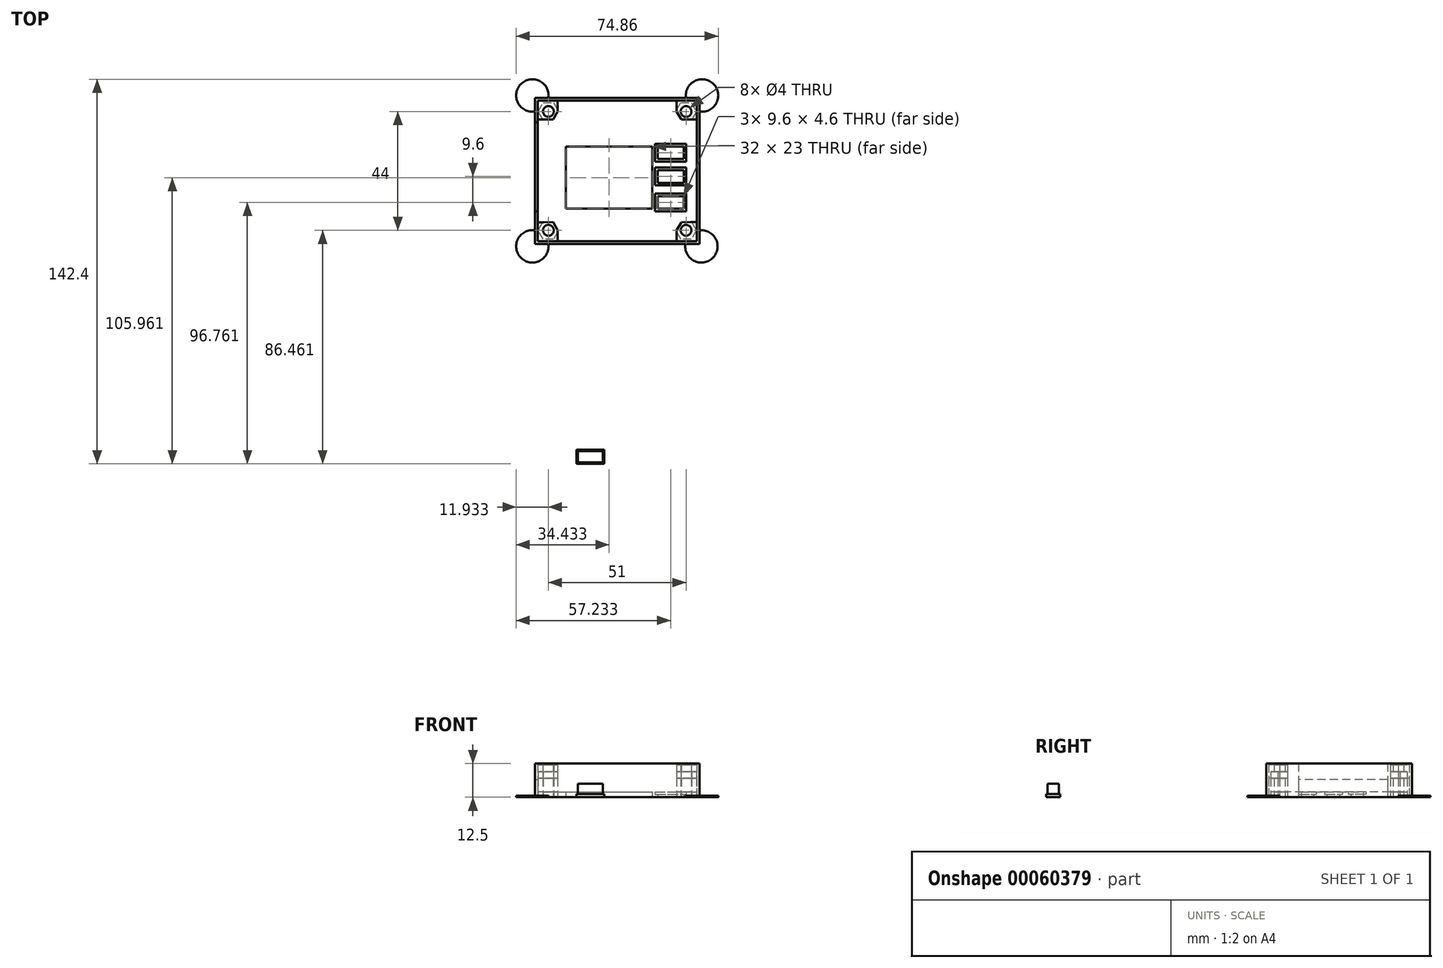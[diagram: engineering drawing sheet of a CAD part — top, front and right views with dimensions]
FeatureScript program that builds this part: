
annotation { "Feature Type Name" : "Feature", "Feature Type Description" : "" }
export const myFeature = defineFeature(function(context is Context, id is Id, definition is map)
    precondition{}
    {
        {
            var Q0;
            Q0=qCreatedBy(makeId("Top.planeOp"),FACE);
            var sketch = newSketch(context, id + "F0", { "sketchPlane" : qUnion([Q0])});
            skCircle(sketch, "E0.cCircle", {"center": v(0, 0) * mm, "radius": 3 * mm, "construction": true});
            skLineSegment(sketch, "E0.0", {"start": v(1.73, 3) * mm, "end": v(3.46, 0) * mm});
            skLineSegment(sketch, "E0.1", {"start": v(3.46, 0) * mm, "end": v(1.74, -3) * mm});
            skLineSegment(sketch, "E0.2", {"start": v(1.74, -3) * mm, "end": v(-1.73, -3) * mm});
            skLineSegment(sketch, "E0.3", {"start": v(-1.73, -3) * mm, "end": v(-3.46, 0) * mm});
            skLineSegment(sketch, "E0.4", {"start": v(-3.46, 0) * mm, "end": v(-1.74, 3) * mm});
            skLineSegment(sketch, "E0.5", {"start": v(-1.74, 3) * mm, "end": v(1.73, 3) * mm});
            skPoint(sketch, "E0.0.midPoint", {"position": v(2.6, 1.5) * mm});
            skCircle(sketch, "E1", {"center": v(0, 0) * mm, "radius": 1.5 * mm});
            skLineSegment(sketch, "E2.bottom", {"start": v(-2.76, 81.41) * mm, "end": v(56.24, 81.41) * mm});
            skLineSegment(sketch, "E2.top", {"start": v(-2.76, 29.41) * mm, "end": v(56.24, 29.41) * mm});
            skLineSegment(sketch, "E2.left", {"start": v(-2.76, 81.41) * mm, "end": v(-2.76, 29.41) * mm});
            skLineSegment(sketch, "E2.right", {"start": v(56.24, 81.41) * mm, "end": v(56.24, 29.41) * mm});
            skPoint(sketch, "E3.0.midPoint", {"position": v(3.84, 78.92) * mm});
            skLineSegment(sketch, "E3.3", {"start": v(-0.48, 74.4) * mm, "end": v(-2.22, 77.4) * mm, "construction": true});
            skLineSegment(sketch, "E3.2", {"start": v(2.98, 74.41) * mm, "end": v(-0.48, 74.4) * mm});
            skLineSegment(sketch, "E3.1", {"start": v(4.7, 77.42) * mm, "end": v(2.98, 74.41) * mm});
            skLineSegment(sketch, "E3.0", {"start": v(2.97, 80.41) * mm, "end": v(4.7, 77.42) * mm, "construction": true});
            skLineSegment(sketch, "E3.4", {"start": v(-2.22, 77.4) * mm, "end": v(-0.5, 80.4) * mm, "construction": true});
            skLineSegment(sketch, "E3.5", {"start": v(-0.5, 80.4) * mm, "end": v(2.97, 80.41) * mm, "construction": true});
            skCircle(sketch, "E4", {"center": v(1.24, 77.41) * mm, "radius": 1.5 * mm, "construction": true});
            skCircle(sketch, "E3.cCircle", {"center": v(1.24, 77.41) * mm, "radius": 3 * mm, "construction": true});
            skPoint(sketch, "E5.0.midPoint", {"position": v(3.84, 34.92) * mm});
            skLineSegment(sketch, "E5.3", {"start": v(-0.48, 30.4) * mm, "end": v(-2.22, 33.4) * mm, "construction": true});
            skLineSegment(sketch, "E5.2", {"start": v(2.98, 30.41) * mm, "end": v(-0.48, 30.4) * mm, "construction": true});
            skLineSegment(sketch, "E5.1", {"start": v(4.7, 33.42) * mm, "end": v(2.98, 30.41) * mm, "construction": true});
            skLineSegment(sketch, "E5.0", {"start": v(2.97, 36.41) * mm, "end": v(4.7, 33.42) * mm});
            skLineSegment(sketch, "E5.4", {"start": v(-2.22, 33.4) * mm, "end": v(-0.5, 36.4) * mm, "construction": true});
            skLineSegment(sketch, "E5.5", {"start": v(-0.5, 36.4) * mm, "end": v(2.97, 36.41) * mm});
            skCircle(sketch, "E6", {"center": v(1.24, 33.41) * mm, "radius": 1.5 * mm, "construction": true});
            skCircle(sketch, "E5.cCircle", {"center": v(1.24, 33.41) * mm, "radius": 3 * mm, "construction": true});
            skPoint(sketch, "E7.0.midPoint", {"position": v(54.84, 78.92) * mm});
            skLineSegment(sketch, "E7.3", {"start": v(50.52, 74.4) * mm, "end": v(48.78, 77.4) * mm});
            skLineSegment(sketch, "E7.2", {"start": v(53.98, 74.41) * mm, "end": v(50.52, 74.4) * mm});
            skLineSegment(sketch, "E7.1", {"start": v(55.7, 77.42) * mm, "end": v(53.98, 74.41) * mm, "construction": true});
            skLineSegment(sketch, "E7.0", {"start": v(53.97, 80.41) * mm, "end": v(55.7, 77.42) * mm, "construction": true});
            skLineSegment(sketch, "E7.4", {"start": v(48.78, 77.4) * mm, "end": v(50.5, 80.4) * mm, "construction": true});
            skLineSegment(sketch, "E7.5", {"start": v(50.5, 80.4) * mm, "end": v(53.97, 80.41) * mm, "construction": true});
            skCircle(sketch, "E8", {"center": v(52.24, 77.41) * mm, "radius": 1.5 * mm, "construction": true});
            skCircle(sketch, "E7.cCircle", {"center": v(52.24, 77.41) * mm, "radius": 3 * mm, "construction": true});
            skPoint(sketch, "E9.0.midPoint", {"position": v(54.84, 34.92) * mm});
            skLineSegment(sketch, "E9.3", {"start": v(50.52, 30.4) * mm, "end": v(48.78, 33.4) * mm, "construction": true});
            skLineSegment(sketch, "E9.2", {"start": v(53.98, 30.41) * mm, "end": v(50.52, 30.4) * mm, "construction": true});
            skLineSegment(sketch, "E9.1", {"start": v(55.7, 33.42) * mm, "end": v(53.98, 30.41) * mm, "construction": true});
            skLineSegment(sketch, "E9.0", {"start": v(53.97, 36.41) * mm, "end": v(55.7, 33.42) * mm, "construction": true});
            skLineSegment(sketch, "E9.4", {"start": v(48.78, 33.4) * mm, "end": v(50.5, 36.4) * mm});
            skLineSegment(sketch, "E9.5", {"start": v(50.5, 36.4) * mm, "end": v(53.97, 36.41) * mm});
            skCircle(sketch, "E10", {"center": v(52.24, 33.41) * mm, "radius": 1.5 * mm, "construction": true});
            skCircle(sketch, "E9.cCircle", {"center": v(52.24, 33.41) * mm, "radius": 3 * mm, "construction": true});
            skLineSegment(sketch, "E11", {"start": v(48.78, 33.4) * mm, "end": v(48.78, 29.41) * mm});
            skLineSegment(sketch, "E12", {"start": v(53.97, 36.41) * mm, "end": v(56.24, 36.41) * mm});
            skCircle(sketch, "E13.0", {"center": v(52.24, 33.41) * mm, "radius": 2 * mm});
            skLineSegment(sketch, "E14.0", {"start": v(50.34, 30.1) * mm, "end": v(48.52, 33.25) * mm});
            skLineSegment(sketch, "E14.1", {"start": v(54.15, 30.11) * mm, "end": v(50.34, 30.1) * mm});
            skLineSegment(sketch, "E14.2", {"start": v(56.05, 33.42) * mm, "end": v(54.15, 30.11) * mm});
            skLineSegment(sketch, "E14.3", {"start": v(54.23, 36.56) * mm, "end": v(56.05, 33.42) * mm});
            skLineSegment(sketch, "E15", {"start": v(4.7, 33.42) * mm, "end": v(4.7, 29.41) * mm});
            skLineSegment(sketch, "E16", {"start": v(-0.5, 36.4) * mm, "end": v(-2.76, 36.4) * mm});
            skLineSegment(sketch, "E17", {"start": v(-0.48, 74.4) * mm, "end": v(-2.76, 74.4) * mm});
            skLineSegment(sketch, "E18", {"start": v(4.7, 77.42) * mm, "end": v(4.7, 81.41) * mm});
            skLineSegment(sketch, "E19", {"start": v(53.98, 74.41) * mm, "end": v(56.24, 74.42) * mm});
            skLineSegment(sketch, "E20", {"start": v(48.78, 77.4) * mm, "end": v(48.78, 81.41) * mm});
            skCircle(sketch, "E21.0", {"center": v(52.24, 77.41) * mm, "radius": 2 * mm});
            skCircle(sketch, "E22.0", {"center": v(1.24, 77.41) * mm, "radius": 2 * mm});
            skCircle(sketch, "E23.0", {"center": v(1.24, 33.41) * mm, "radius": 2 * mm});
            skLineSegment(sketch, "E24.0", {"start": v(3.14, 80.71) * mm, "end": v(4.97, 77.57) * mm});
            skLineSegment(sketch, "E24.1", {"start": v(-0.67, 80.7) * mm, "end": v(3.14, 80.71) * mm});
            skLineSegment(sketch, "E24.2", {"start": v(-2.57, 77.4) * mm, "end": v(-0.67, 80.7) * mm});
            skLineSegment(sketch, "E24.3", {"start": v(-0.74, 74.26) * mm, "end": v(-2.57, 77.4) * mm});
            skLineSegment(sketch, "E25.0", {"start": v(-2.57, 33.4) * mm, "end": v(-0.76, 36.56) * mm});
            skLineSegment(sketch, "E25.1", {"start": v(-0.66, 30.1) * mm, "end": v(-2.57, 33.4) * mm});
            skLineSegment(sketch, "E25.2", {"start": v(3.15, 30.11) * mm, "end": v(-0.66, 30.1) * mm});
            skLineSegment(sketch, "E25.3", {"start": v(4.97, 33.27) * mm, "end": v(3.15, 30.11) * mm});
            skLineSegment(sketch, "E26.0", {"start": v(56.05, 77.42) * mm, "end": v(44.73, 57.73) * mm});
            skLineSegment(sketch, "E26.1", {"start": v(54.14, 80.71) * mm, "end": v(56.05, 77.42) * mm});
            skLineSegment(sketch, "E26.2", {"start": v(50.33, 80.7) * mm, "end": v(54.14, 80.71) * mm});
            skLineSegment(sketch, "E26.3", {"start": v(48.52, 77.55) * mm, "end": v(50.33, 80.7) * mm});
            skPoint(sketch, "E27", {"position": v(7.74, 41.41) * mm});
            skLineSegment(sketch, "E28.bottom", {"start": v(7.74, 41.41) * mm, "end": v(39.74, 41.41) * mm});
            skLineSegment(sketch, "E28.top", {"start": v(7.74, 64.41) * mm, "end": v(39.74, 64.41) * mm});
            skLineSegment(sketch, "E28.left", {"start": v(7.74, 41.41) * mm, "end": v(7.74, 64.41) * mm});
            skLineSegment(sketch, "E28.right", {"start": v(39.74, 41.41) * mm, "end": v(39.74, 64.41) * mm});
            skPoint(sketch, "E29", {"position": v(41.74, 64.41) * mm});
            skLineSegment(sketch, "E30.bottom", {"start": v(41.74, 64.41) * mm, "end": v(51.34, 64.41) * mm});
            skLineSegment(sketch, "E30.top", {"start": v(41.74, 59.81) * mm, "end": v(51.34, 59.81) * mm});
            skLineSegment(sketch, "E30.left", {"start": v(41.74, 64.41) * mm, "end": v(41.74, 59.81) * mm});
            skLineSegment(sketch, "E30.right", {"start": v(51.34, 64.41) * mm, "end": v(51.34, 59.81) * mm});
            skLineSegment(sketch, "E31.bottom", {"start": v(41.74, 41.41) * mm, "end": v(51.34, 41.41) * mm});
            skLineSegment(sketch, "E31.top", {"start": v(41.74, 46.01) * mm, "end": v(51.34, 46.01) * mm});
            skLineSegment(sketch, "E31.left", {"start": v(41.74, 41.41) * mm, "end": v(41.74, 46.01) * mm});
            skLineSegment(sketch, "E31.right", {"start": v(51.34, 41.41) * mm, "end": v(51.34, 46.01) * mm});
            skLineSegment(sketch, "E32.bottom", {"start": v(41.74, 51.01) * mm, "end": v(51.34, 51.01) * mm});
            skLineSegment(sketch, "E32.top", {"start": v(41.74, 55.61) * mm, "end": v(51.34, 55.61) * mm});
            skLineSegment(sketch, "E32.left", {"start": v(41.74, 51.01) * mm, "end": v(41.74, 55.61) * mm});
            skLineSegment(sketch, "E32.right", {"start": v(51.34, 51.01) * mm, "end": v(51.34, 55.61) * mm});
            skLineSegment(sketch, "E33.0", {"start": v(-3.76, 82.41) * mm, "end": v(-3.76, 28.41) * mm});
            skLineSegment(sketch, "E33.1", {"start": v(-3.76, 82.41) * mm, "end": v(57.24, 82.41) * mm});
            skLineSegment(sketch, "E33.2", {"start": v(57.24, 82.41) * mm, "end": v(57.24, 28.41) * mm});
            skLineSegment(sketch, "E33.3", {"start": v(-3.76, 28.41) * mm, "end": v(57.24, 28.41) * mm});
            skPoint(sketch, "E34", {"position": v(-3.76, 73.41) * mm});
            skPoint(sketch, "E35", {"position": v(-3.76, 40.41) * mm});
            skLineSegment(sketch, "E36", {"start": v(-3.76, 73.41) * mm, "end": v(-2.76, 73.41) * mm});
            skLineSegment(sketch, "E37", {"start": v(-3.76, 40.41) * mm, "end": v(-2.76, 40.41) * mm});
            skLineSegment(sketch, "E38.bottom", {"start": v(13.09, -34.33) * mm, "end": v(22.29, -34.33) * mm});
            skLineSegment(sketch, "E38.top", {"start": v(13.09, -38.53) * mm, "end": v(22.29, -38.53) * mm});
            skLineSegment(sketch, "E38.left", {"start": v(13.09, -34.33) * mm, "end": v(13.09, -38.53) * mm});
            skLineSegment(sketch, "E38.right", {"start": v(22.29, -34.33) * mm, "end": v(22.29, -38.53) * mm});
            skLineSegment(sketch, "E39.0", {"start": v(12.09, -33.33) * mm, "end": v(23.29, -33.33) * mm});
            skLineSegment(sketch, "E39.1", {"start": v(12.09, -33.33) * mm, "end": v(12.09, -39.53) * mm});
            skLineSegment(sketch, "E39.2", {"start": v(12.09, -39.53) * mm, "end": v(23.29, -39.53) * mm});
            skLineSegment(sketch, "E39.3", {"start": v(23.29, -33.33) * mm, "end": v(23.29, -39.53) * mm});
            skLineSegment(sketch, "E40.bottom", {"start": v(12.2, -48.35) * mm, "end": v(21.4, -48.35) * mm});
            skLineSegment(sketch, "E40.top", {"start": v(12.2, -52.55) * mm, "end": v(21.4, -52.55) * mm});
            skLineSegment(sketch, "E40.left", {"start": v(12.2, -48.35) * mm, "end": v(12.2, -52.55) * mm});
            skLineSegment(sketch, "E40.right", {"start": v(21.4, -48.35) * mm, "end": v(21.4, -52.55) * mm});
            skLineSegment(sketch, "E41.0", {"start": v(11.7, -47.85) * mm, "end": v(21.9, -47.85) * mm});
            skLineSegment(sketch, "E41.1", {"start": v(11.7, -47.85) * mm, "end": v(11.7, -53.05) * mm});
            skLineSegment(sketch, "E41.2", {"start": v(11.7, -53.05) * mm, "end": v(21.9, -53.05) * mm});
            skLineSegment(sketch, "E41.3", {"start": v(21.9, -47.85) * mm, "end": v(21.9, -53.05) * mm});
            skArc(sketch, "E42", {"start": v(57.24, 77.42) * mm, "mid": v(62.4, 87.6) * mm, "end": v(52.24, 82.41) * mm});
            skArc(sketch, "E43", {"start": v(52.24, 29.41) * mm, "mid": v(61.67, 22.77) * mm, "end": v(57.24, 33.42) * mm});
            skArc(sketch, "E44", {"start": v(-3.76, 33.4) * mm, "mid": v(-8.92, 23.23) * mm, "end": v(1.24, 28.41) * mm});
            skArc(sketch, "E45", {"start": v(1.24, 82.41) * mm, "mid": v(-8.93, 87.57) * mm, "end": v(-3.76, 77.4) * mm});
            skLineSegment(sketch, "E46.0", {"start": v(40.74, 58.81) * mm, "end": v(52.34, 58.81) * mm});
            skLineSegment(sketch, "E46.1", {"start": v(40.74, 65.41) * mm, "end": v(40.74, 58.81) * mm});
            skLineSegment(sketch, "E46.2", {"start": v(40.74, 65.41) * mm, "end": v(52.34, 65.41) * mm});
            skLineSegment(sketch, "E46.3", {"start": v(52.34, 65.41) * mm, "end": v(52.34, 58.81) * mm});
            skLineSegment(sketch, "E47.0", {"start": v(40.74, 56.61) * mm, "end": v(52.34, 56.61) * mm});
            skLineSegment(sketch, "E47.1", {"start": v(40.74, 50.01) * mm, "end": v(40.74, 56.61) * mm});
            skLineSegment(sketch, "E47.2", {"start": v(40.74, 50.01) * mm, "end": v(52.34, 50.01) * mm});
            skLineSegment(sketch, "E47.3", {"start": v(52.34, 50.01) * mm, "end": v(52.34, 56.61) * mm});
            skLineSegment(sketch, "E48.0", {"start": v(40.74, 47.01) * mm, "end": v(52.34, 47.01) * mm});
            skLineSegment(sketch, "E48.1", {"start": v(40.74, 40.41) * mm, "end": v(40.74, 47.01) * mm});
            skLineSegment(sketch, "E48.2", {"start": v(40.74, 40.41) * mm, "end": v(52.34, 40.41) * mm});
            skLineSegment(sketch, "E48.3", {"start": v(52.34, 40.41) * mm, "end": v(52.34, 47.01) * mm});
            skLineSegment(sketch, "E49", {"start": v(0.74, 37.41) * mm, "end": v(52.74, 37.41) * mm, "construction": true});
            skLineSegment(sketch, "E50", {"start": v(52.74, 37.41) * mm, "end": v(52.74, 73.41) * mm, "construction": true});
            skLineSegment(sketch, "E51", {"start": v(52.74, 73.41) * mm, "end": v(0.74, 73.41) * mm, "construction": true});
            skLineSegment(sketch, "E52", {"start": v(0.74, 73.41) * mm, "end": v(0.74, 37.41) * mm, "construction": true});
            skArc(sketch, "E53", {"start": v(0.74, 55.41) * mm, "mid": v(-2.26, 52.41) * mm, "end": v(0.74, 49.41) * mm, "construction": true});
            skArc(sketch, "E54", {"start": v(52.74, 49.41) * mm, "mid": v(55.74, 52.41) * mm, "end": v(52.74, 55.41) * mm, "construction": true});
            skSolve(sketch);
        }
        {
            var Q0;
            {var subQ12=sQuery(id+"F0.wireOp",EDGE,"E14.1");Q0=makeQuery(id+"F0.imprint","IMPRINT",FACE,{"disambiguationData":[TD([[makeQuery(id+"F0.imprint","IMPRINT",EDGE,{"derivedFrom":subQ12}),1.0]])]});}
            var Q1;
            {var subQ6=sQuery(id+"F0.wireOp",EDGE,"E9.4");Q1=makeQuery(id+"F0.imprint","IMPRINT",FACE,{"disambiguationData":[TD([[makeQuery(id+"F0.imprint","IMPRINT",EDGE,{"derivedFrom":subQ6}),-1.0]])]});}
            var Q2;
            {var subQ5=sQuery(id+"F0.wireOp",EDGE,"E25.1");Q2=makeQuery(id+"F0.imprint","IMPRINT",FACE,{"disambiguationData":[TD([[makeQuery(id+"F0.imprint","IMPRINT",EDGE,{"derivedFrom":subQ5}),1.0]])]});}
            var Q3;
            {var subQ5=sQuery(id+"F0.wireOp",EDGE,"E5.0");Q3=makeQuery(id+"F0.imprint","IMPRINT",FACE,{"disambiguationData":[TD([[makeQuery(id+"F0.imprint","IMPRINT",EDGE,{"derivedFrom":subQ5}),-1.0]])]});}
            var Q4;
            {var subQ11=sQuery(id+"F0.wireOp",EDGE,"E24.1");Q4=makeQuery(id+"F0.imprint","IMPRINT",FACE,{"disambiguationData":[TD([[makeQuery(id+"F0.imprint","IMPRINT",EDGE,{"derivedFrom":subQ11}),1.0]])]});}
            var Q5;
            {var subQ5=sQuery(id+"F0.wireOp",EDGE,"E3.2");Q5=makeQuery(id+"F0.imprint","IMPRINT",FACE,{"disambiguationData":[TD([[makeQuery(id+"F0.imprint","IMPRINT",EDGE,{"derivedFrom":subQ5}),-1.0]])]});}
            var Q6;
            {var subQ7=sQuery(id+"F0.wireOp",EDGE,"E26.1");Q6=makeQuery(id+"F0.imprint","IMPRINT",FACE,{"disambiguationData":[TD([[makeQuery(id+"F0.imprint","IMPRINT",EDGE,{"derivedFrom":subQ7}),1.0]])]});}
            var Q7;
            {var subQ1=sQuery(id+"F0.wireOp",EDGE,"E7.3");Q7=makeQuery(id+"F0.imprint","IMPRINT",FACE,{"disambiguationData":[TD([[makeQuery(id+"F0.imprint","IMPRINT",EDGE,{"derivedFrom":subQ1}),-1.0]])]});}
            extrude(context, id + "F1", {"entities" : qUnion([Q0, Q1, Q2, Q3, Q4, Q5, Q6, Q7]), "depth" : 7 * mm});
        }
        {
            var Q0;
            {var subQ12=sQuery(id+"F0.wireOp",EDGE,"E14.1");Q0=makeQuery(id+"F0.imprint","IMPRINT",FACE,{"disambiguationData":[TD([[makeQuery(id+"F0.imprint","IMPRINT",EDGE,{"derivedFrom":subQ12}),1.0]])]});}
            var Q1;
            {var subQ7=sQuery(id+"F0.wireOp",EDGE,"E26.1");Q1=makeQuery(id+"F0.imprint","IMPRINT",FACE,{"disambiguationData":[TD([[makeQuery(id+"F0.imprint","IMPRINT",EDGE,{"derivedFrom":subQ7}),1.0]])]});}
            var Q2;
            {var subQ11=sQuery(id+"F0.wireOp",EDGE,"E24.1");Q2=makeQuery(id+"F0.imprint","IMPRINT",FACE,{"disambiguationData":[TD([[makeQuery(id+"F0.imprint","IMPRINT",EDGE,{"derivedFrom":subQ11}),1.0]])]});}
            var Q3;
            {var subQ5=sQuery(id+"F0.wireOp",EDGE,"E25.1");Q3=makeQuery(id+"F0.imprint","IMPRINT",FACE,{"disambiguationData":[TD([[makeQuery(id+"F0.imprint","IMPRINT",EDGE,{"derivedFrom":subQ5}),1.0]])]});}
            extrude(context, id + "F2", {"entities" : qUnion([Q0, Q1, Q2, Q3]), "endBound" : BoundingType.UP_TO_NEXT, "depth" : 25 * mm});
        }
        {
            var Q0;
            Q0=makeQuery(id+"F2.opExtrude","CAP_FACE",FACE,{"disambiguationData":[OSD([sQuery(id+"F0.wireOp",EDGE,"E2.top"),sQuery(id+"F0.wireOp",EDGE,"E2.right"),sQuery(id+"F0.wireOp",EDGE,"E9.4"),sQuery(id+"F0.wireOp",EDGE,"E9.5"),sQuery(id+"F0.wireOp",EDGE,"E11"),sQuery(id+"F0.wireOp",EDGE,"E12"),sQuery(id+"F0.wireOp",EDGE,"E13.0")])],"isStart":false});
            var Q1;
            Q1=makeQuery(id+"F2.opExtrude","CAP_FACE",FACE,{"disambiguationData":[OSD([sQuery(id+"F0.wireOp",EDGE,"E2.top"),sQuery(id+"F0.wireOp",EDGE,"E2.left"),sQuery(id+"F0.wireOp",EDGE,"E5.0"),sQuery(id+"F0.wireOp",EDGE,"E5.5"),sQuery(id+"F0.wireOp",EDGE,"E15"),sQuery(id+"F0.wireOp",EDGE,"E16"),sQuery(id+"F0.wireOp",EDGE,"E23.0")])],"isStart":false});
            var Q2;
            Q2=makeQuery(id+"F2.opExtrude","CAP_FACE",FACE,{"disambiguationData":[OSD([sQuery(id+"F0.wireOp",EDGE,"E2.bottom"),sQuery(id+"F0.wireOp",EDGE,"E2.left"),sQuery(id+"F0.wireOp",EDGE,"E3.2"),sQuery(id+"F0.wireOp",EDGE,"E3.1"),sQuery(id+"F0.wireOp",EDGE,"E17"),sQuery(id+"F0.wireOp",EDGE,"E18"),sQuery(id+"F0.wireOp",EDGE,"E22.0")])],"isStart":false});
            var Q3;
            Q3=makeQuery(id+"F2.opExtrude","CAP_FACE",FACE,{"disambiguationData":[OSD([sQuery(id+"F0.wireOp",EDGE,"E2.bottom"),sQuery(id+"F0.wireOp",EDGE,"E2.right"),sQuery(id+"F0.wireOp",EDGE,"E7.3"),sQuery(id+"F0.wireOp",EDGE,"E7.2"),sQuery(id+"F0.wireOp",EDGE,"E19"),sQuery(id+"F0.wireOp",EDGE,"E20"),sQuery(id+"F0.wireOp",EDGE,"E21.0")])],"isStart":false});
            extrude(context, id + "F3", {"entities" : qUnion([Q0, Q1, Q2, Q3]), "depth" : 2.5 * mm});
        }
        {
            var Q0;
            Q0=makeQuery(id+"F1.opExtrude","CAP_FACE",FACE,{"disambiguationData":[OSD([sQuery(id+"F0.wireOp",EDGE,"E2.top"),sQuery(id+"F0.wireOp",EDGE,"E2.right"),sQuery(id+"F0.wireOp",EDGE,"E9.4"),sQuery(id+"F0.wireOp",EDGE,"E9.5"),sQuery(id+"F0.wireOp",EDGE,"E11"),sQuery(id+"F0.wireOp",EDGE,"E12"),sQuery(id+"F0.wireOp",EDGE,"E13.0")])],"isStart":false});
            var Q1;
            Q1=makeQuery(id+"F1.opExtrude","CAP_FACE",FACE,{"disambiguationData":[OSD([sQuery(id+"F0.wireOp",EDGE,"E2.top"),sQuery(id+"F0.wireOp",EDGE,"E2.left"),sQuery(id+"F0.wireOp",EDGE,"E5.0"),sQuery(id+"F0.wireOp",EDGE,"E5.5"),sQuery(id+"F0.wireOp",EDGE,"E15"),sQuery(id+"F0.wireOp",EDGE,"E16"),sQuery(id+"F0.wireOp",EDGE,"E23.0")])],"isStart":false});
            var Q2;
            Q2=makeQuery(id+"F1.opExtrude","CAP_FACE",FACE,{"disambiguationData":[OSD([sQuery(id+"F0.wireOp",EDGE,"E2.bottom"),sQuery(id+"F0.wireOp",EDGE,"E2.left"),sQuery(id+"F0.wireOp",EDGE,"E3.2"),sQuery(id+"F0.wireOp",EDGE,"E3.1"),sQuery(id+"F0.wireOp",EDGE,"E17"),sQuery(id+"F0.wireOp",EDGE,"E18"),sQuery(id+"F0.wireOp",EDGE,"E22.0")])],"isStart":false});
            var Q3;
            Q3=makeQuery(id+"F1.opExtrude","CAP_FACE",FACE,{"disambiguationData":[OSD([sQuery(id+"F0.wireOp",EDGE,"E2.bottom"),sQuery(id+"F0.wireOp",EDGE,"E2.right"),sQuery(id+"F0.wireOp",EDGE,"E7.3"),sQuery(id+"F0.wireOp",EDGE,"E7.2"),sQuery(id+"F0.wireOp",EDGE,"E19"),sQuery(id+"F0.wireOp",EDGE,"E20"),sQuery(id+"F0.wireOp",EDGE,"E21.0")])],"isStart":false});
            extrude(context, id + "F4", {"entities" : qUnion([Q0, Q1, Q2, Q3]), "operationType" : NewBodyOperationType.ADD, "depth" : 5 * mm, "hasSecondDirection" : true, "secondDirectionOppositeDirection" : false, "secondDirectionDepth" : 2.5 * mm});
        }
        {
            var Q0;
            {var subQ14=sQuery(id+"F0.wireOp",EDGE,"E3.2");Q0=makeQuery(id+"F0.imprint","IMPRINT",FACE,{"disambiguationData":[TD([[makeQuery(id+"F0.imprint","IMPRINT",EDGE,{"derivedFrom":subQ14}),1.0]])]});}
            var Q1;
            Q1=makeQuery(id+"F0.imprint","IMPRINT",FACE,{"disambiguationData":[TD([[makeQuery(id+"F0.imprint","IMPRINT",EDGE,{"derivedFrom":sQuery(id+"F0.wireOp",EDGE,"E22.0")}),1.0]])]});
            var Q2;
            Q2=makeQuery(id+"F0.imprint","IMPRINT",FACE,{"disambiguationData":[TD([[makeQuery(id+"F0.imprint","IMPRINT",EDGE,{"derivedFrom":sQuery(id+"F0.wireOp",EDGE,"E21.0")}),1.0]])]});
            var Q3;
            Q3=makeQuery(id+"F0.imprint","IMPRINT",FACE,{"disambiguationData":[TD([[makeQuery(id+"F0.imprint","IMPRINT",EDGE,{"derivedFrom":sQuery(id+"F0.wireOp",EDGE,"E13.0")}),1.0]])]});
            var Q4;
            Q4=makeQuery(id+"F0.imprint","IMPRINT",FACE,{"disambiguationData":[TD([[makeQuery(id+"F0.imprint","IMPRINT",EDGE,{"derivedFrom":sQuery(id+"F0.wireOp",EDGE,"E23.0")}),1.0]])]});
            extrude(context, id + "F5", {"entities" : qUnion([Q0, Q1, Q2, Q3, Q4]), "depth" : 2 * mm});
        }
        {
            var Q0;
            Q0=makeQuery(id+"F0.imprint","IMPRINT",FACE,{"disambiguationData":[TD([[makeQuery(id+"F0.imprint","IMPRINT",EDGE,{"derivedFrom":sQuery(id+"F0.wireOp",EDGE,"E30.bottom")}),1.0]])]});
            var Q1;
            Q1=makeQuery(id+"F0.imprint","IMPRINT",FACE,{"disambiguationData":[TD([[makeQuery(id+"F0.imprint","IMPRINT",EDGE,{"derivedFrom":sQuery(id+"F0.wireOp",EDGE,"E32.bottom")}),-1.0]])]});
            var Q2;
            Q2=makeQuery(id+"F0.imprint","IMPRINT",FACE,{"disambiguationData":[TD([[makeQuery(id+"F0.imprint","IMPRINT",EDGE,{"derivedFrom":sQuery(id+"F0.wireOp",EDGE,"E31.bottom")}),-1.0]])]});
            extrude(context, id + "F6", {"entities" : qUnion([Q0, Q1, Q2]), "operationType" : NewBodyOperationType.ADD, "depth" : 1 * mm});
        }
        {
            var Q0;
            {var subQ18=sQuery(id+"F0.wireOp",EDGE,"E33.1");Q0=makeQuery(id+"F0.imprint","IMPRINT",FACE,{"disambiguationData":[TD([[makeQuery(id+"F0.imprint","IMPRINT",EDGE,{"derivedFrom":subQ18}),-1.0]])]});}
            var Q1;
            {var subQ0=sQuery(id+"F0.wireOp",EDGE,"E37");Q1=makeQuery(id+"F0.imprint","IMPRINT",FACE,{"disambiguationData":[TD([[makeQuery(id+"F0.imprint","IMPRINT",EDGE,{"derivedFrom":subQ0}),-1.0]])]});}
            extrude(context, id + "F7", {"entities" : qUnion([Q0, Q1]), "depth" : 12.5 * mm});
        }
        {
            var Q0;
            {var subQ0=sQuery(id+"F0.wireOp",EDGE,"E36");Q0=makeQuery(id+"F0.imprint","IMPRINT",FACE,{"disambiguationData":[TD([[makeQuery(id+"F0.imprint","IMPRINT",EDGE,{"derivedFrom":subQ0}),-1.0]])]});}
            extrude(context, id + "F8", {"entities" : qUnion([Q0]), "depth" : 6.5 * mm});
        }
        {
            var Q0;
            Q0=makeQuery(id+"F0.imprint","IMPRINT",FACE,{"disambiguationData":[TD([[makeQuery(id+"F0.imprint","IMPRINT",EDGE,{"derivedFrom":sQuery(id+"F0.wireOp",EDGE,"E40.bottom")}),1.0]])]});
            extrude(context, id + "F9", {"entities" : qUnion([Q0]), "depth" : 1.2 * mm});
        }
        {
            var Q0;
            Q0=makeQuery(id+"F0.imprint","IMPRINT",FACE,{"disambiguationData":[TD([[makeQuery(id+"F0.imprint","IMPRINT",EDGE,{"derivedFrom":sQuery(id+"F0.wireOp",EDGE,"E40.bottom")}),-1.0]])]});
            extrude(context, id + "F10", {"entities" : qUnion([Q0]), "operationType" : NewBodyOperationType.ADD, "depth" : 5 * mm});
        }
        {
            var Q0;
            {var subQ3=sQuery(id+"F0.wireOp",EDGE,"E44");Q0=makeQuery(id+"F0.imprint","IMPRINT",FACE,{"disambiguationData":[TD([[makeQuery(id+"F0.imprint","IMPRINT",EDGE,{"derivedFrom":subQ3}),1.0]])]});}
            var Q1;
            {var subQ3=sQuery(id+"F0.wireOp",EDGE,"E45");Q1=makeQuery(id+"F0.imprint","IMPRINT",FACE,{"disambiguationData":[TD([[makeQuery(id+"F0.imprint","IMPRINT",EDGE,{"derivedFrom":subQ3}),1.0]])]});}
            var Q2;
            {var subQ3=sQuery(id+"F0.wireOp",EDGE,"E42");Q2=makeQuery(id+"F0.imprint","IMPRINT",FACE,{"disambiguationData":[TD([[makeQuery(id+"F0.imprint","IMPRINT",EDGE,{"derivedFrom":subQ3}),1.0]])]});}
            var Q3;
            {var subQ0=sQuery(id+"F0.wireOp",EDGE,"E33.3");var subQ1=sQuery(id+"F0.wireOp",EDGE,"E33.2");var subQ2=makeQuery(id+"F0.imprint","INTERSECT",VERTEX,{"derivedFrom":[subQ1,subQ0]});Q3=makeQuery(id+"F0.imprint","IMPRINT",FACE,{"disambiguationData":[TD([[makeQuery(id+"F0.imprint","IMPRINT",EDGE,{"disambiguationData":[TD([[subQ2,1.0]])],"derivedFrom":subQ1}),1.0]])]});}
            extrude(context, id + "F11", {"entities" : qUnion([Q0, Q1, Q2, Q3]), "operationType" : NewBodyOperationType.ADD, "depth" : 0.5 * mm});
        }
    });
